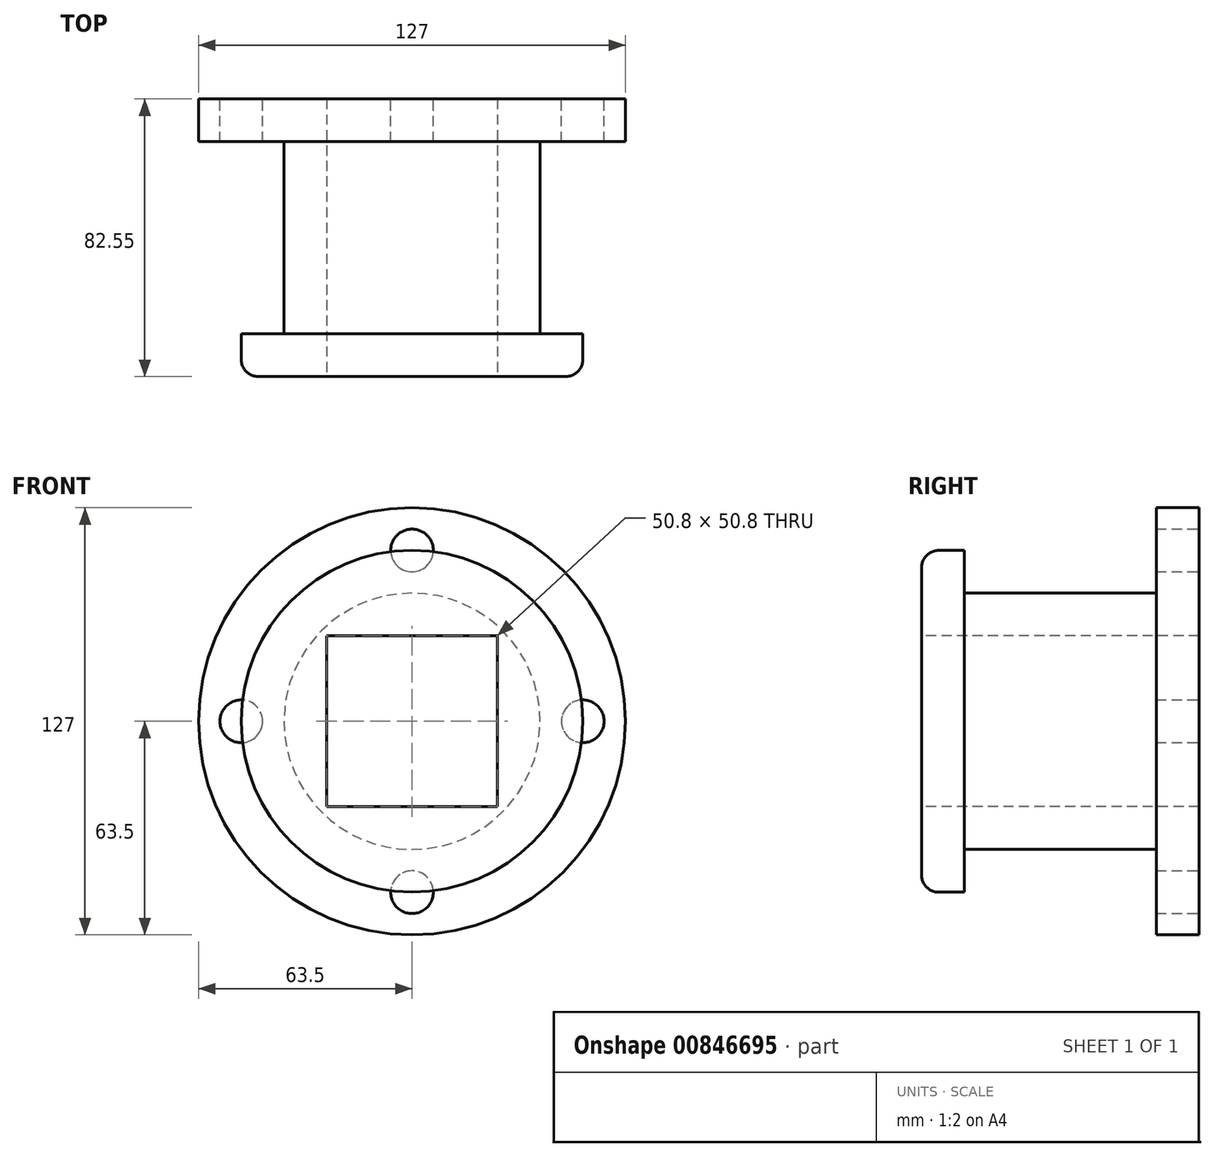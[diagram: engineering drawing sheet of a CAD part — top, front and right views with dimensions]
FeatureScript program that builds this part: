
annotation { "Feature Type Name" : "Feature", "Feature Type Description" : "" }
export const myFeature = defineFeature(function(context is Context, id is Id, definition is map)
    precondition{}
    {
        {
            var Q0;
            Q0=qCreatedBy(makeId("Front.planeOp"),FACE);
            var sketch = newSketch(context, id + "F0", { "sketchPlane" : qUnion([Q0])});
            skCircle(sketch, "E0", {"center": v(0, 0) * mm, "radius": 63.5 * mm});
            skSolve(sketch);
        }
        {
            var Q0;
            Q0 = qSketchRegion(id + "F0", true);
            extrude(context, id + "F1", {"entities" : qUnion([Q0]), "depth" : 12.7 * mm, "offsetDistance" : 25.4 * mm});
        }
        {
            var Q0;
            Q0=makeQuery(id+"F1.opExtrude","CAP_FACE",FACE,{"disambiguationData":[OSD([sQuery(id+"F0.wireOp",EDGE,"E0")])],"isStart":false});
            var sketch = newSketch(context, id + "F2", { "sketchPlane" : qUnion([Q0])});
            skCircle(sketch, "E1", {"center": v(0, 0) * mm, "radius": 38.1 * mm});
            skSolve(sketch);
        }
        {
            var Q0;
            Q0 = qSketchRegion(id + "F2", true);
            extrude(context, id + "F3", {"entities" : qUnion([Q0]), "operationType" : NewBodyOperationType.ADD, "depth" : 57.15 * mm, "offsetDistance" : 25.4 * mm});
        }
        {
            var Q0;
            Q0=makeQuery(id+"F3.opExtrude","CAP_FACE",FACE,{"disambiguationData":[OSD([sQuery(id+"F2.wireOp",EDGE,"E1")])],"isStart":false});
            var sketch = newSketch(context, id + "F4", { "sketchPlane" : qUnion([Q0])});
            skCircle(sketch, "E2", {"center": v(0, 0) * mm, "radius": 50.8 * mm});
            skSolve(sketch);
        }
        {
            var Q0;
            Q0 = qSketchRegion(id + "F4", true);
            extrude(context, id + "F5", {"entities" : qUnion([Q0]), "operationType" : NewBodyOperationType.ADD, "depth" : 12.7 * mm, "offsetDistance" : 25.4 * mm});
        }
        {
            var Q0;
            Q0=makeQuery(id+"F5.opExtrude","CAP_FACE",FACE,{"disambiguationData":[OSD([sQuery(id+"F4.wireOp",EDGE,"E2")])],"isStart":false});
            var sketch = newSketch(context, id + "F6", { "sketchPlane" : qUnion([Q0])});
            skLineSegment(sketch, "E3.bottom", {"start": v(-25.4, 25.4) * mm, "end": v(25.4, 25.4) * mm});
            skLineSegment(sketch, "E3.top", {"start": v(-25.4, -25.4) * mm, "end": v(25.4, -25.4) * mm});
            skLineSegment(sketch, "E3.left", {"start": v(-25.4, 25.4) * mm, "end": v(-25.4, -25.4) * mm});
            skLineSegment(sketch, "E3.right", {"start": v(25.4, 25.4) * mm, "end": v(25.4, -25.4) * mm});
            skPoint(sketch, "E3.middle", {"position": v(0, 0) * mm});
            skSolve(sketch);
        }
        {
            var Q0;
            Q0 = qSketchRegion(id + "F6", true);
            extrude(context, id + "F7", {"entities" : qUnion([Q0]), "operationType" : NewBodyOperationType.REMOVE, "oppositeDirection" : true, "depth" : 82.55 * mm, "offsetDistance" : 25.4 * mm});
        }
        {
            var Q0;
            Q0=makeQuery(id+"F1.opExtrude","CAP_FACE",FACE,{"disambiguationData":[OSD([sQuery(id+"F0.wireOp",EDGE,"E0")])],"isStart":true});
            var sketch = newSketch(context, id + "F8", { "sketchPlane" : qUnion([Q0])});
            skCircle(sketch, "E4", {"center": v(0, 50.8) * mm, "radius": 6.35 * mm});
            skCircle(sketch, "E5", {"center": v(-50.8, 0) * mm, "radius": 6.35 * mm});
            skCircle(sketch, "E6", {"center": v(0, -50.8) * mm, "radius": 6.35 * mm});
            skCircle(sketch, "E7", {"center": v(50.8, 0) * mm, "radius": 6.35 * mm});
            skSolve(sketch);
        }
        {
            var Q0;
            Q0 = qSketchRegion(id + "F8", true);
            extrude(context, id + "F9", {"entities" : qUnion([Q0]), "operationType" : NewBodyOperationType.REMOVE, "oppositeDirection" : true, "depth" : 12.7 * mm, "offsetDistance" : 25.4 * mm});
        }
        {
            var Q0;
            Q0=makeQuery(id+"F5.opExtrude","CAP_EDGE",EDGE,{"disambiguationData":[OSD([sQuery(id+"F4.wireOp",EDGE,"E2")])],"isStart":false});
            fillet(context, id + "F10", {"entities" : qUnion([Q0]), "radius" : 5.08 * mm, "tangentPropagation" : true, "allowEdgeOverflow" : false});
        }
    });
